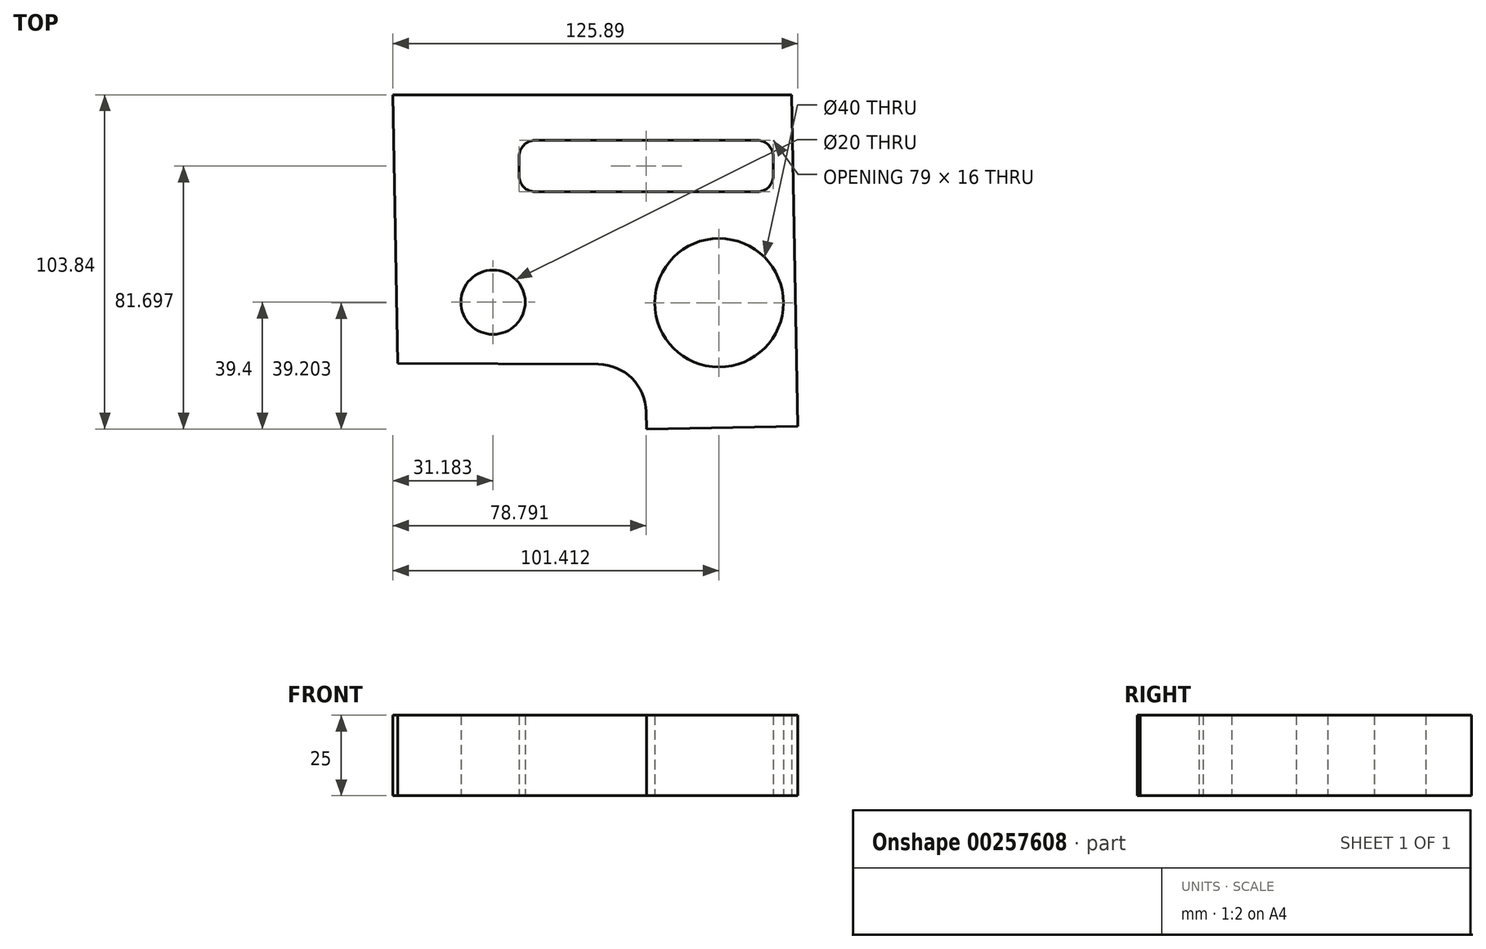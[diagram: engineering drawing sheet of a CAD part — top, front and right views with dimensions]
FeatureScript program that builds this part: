
annotation { "Feature Type Name" : "Feature", "Feature Type Description" : "" }
export const myFeature = defineFeature(function(context is Context, id is Id, definition is map)
    precondition{}
    {
        {
            var Q0;
            Q0=qCreatedBy(makeId("Top.planeOp"),FACE);
            var sketch = newSketch(context, id + "F0", { "sketchPlane" : qUnion([Q0])});
            skLineSegment(sketch, "E0", {"start": v(-101.89, 48.27) * mm, "end": v(22.11, 48.27) * mm});
            skLineSegment(sketch, "E1", {"start": v(22.11, 48.27) * mm, "end": v(24, -54.71) * mm});
            skPoint(sketch, "E2.visualSharp", {"position": v(-0.37, -35.15) * mm});
            skLineSegment(sketch, "E3", {"start": v(-101.89, 48.27) * mm, "end": v(-100.37, -35.15) * mm});
            skLineSegment(sketch, "E4", {"start": v(-101.89, 48.27) * mm, "end": v(-100.7, -16.72) * mm});
            skLineSegment(sketch, "E5", {"start": v(-100.7, -16.72) * mm, "end": v(-70.7, -16.17) * mm});
            skCircle(sketch, "E6", {"center": v(-70.7, -16.17) * mm, "radius": 10 * mm});
            skLineSegment(sketch, "E7", {"start": v(22.11, 48.27) * mm, "end": v(22.66, 18.28) * mm});
            skLineSegment(sketch, "E8", {"start": v(22.11, 48.27) * mm, "end": v(17.16, 48.27) * mm});
            skLineSegment(sketch, "E9", {"start": v(22.11, 48.27) * mm, "end": v(22.37, 34.27) * mm});
            skLineSegment(sketch, "E10", {"start": v(16.4, 29.13) * mm, "end": v(16.4, 23.13) * mm});
            skLineSegment(sketch, "E11", {"start": v(11.4, 18.13) * mm, "end": v(-57.6, 18.13) * mm});
            skLineSegment(sketch, "E12", {"start": v(11.4, 34.13) * mm, "end": v(-57.6, 34.13) * mm});
            skLineSegment(sketch, "E13", {"start": v(-62.6, 29.13) * mm, "end": v(-62.6, 23.13) * mm});
            skPoint(sketch, "E14.visualSharp", {"position": v(-62.6, 34.13) * mm});
            skArc(sketch, "E14.filletArc", {"start": v(-57.6, 34.13) * mm, "mid": v(-61.13, 32.66) * mm, "end": v(-62.6, 29.13) * mm});
            skPoint(sketch, "E15.visualSharp", {"position": v(-62.6, 18.13) * mm});
            skArc(sketch, "E15.filletArc", {"start": v(-62.6, 23.13) * mm, "mid": v(-61.13, 19.6) * mm, "end": v(-57.6, 18.13) * mm});
            skPoint(sketch, "E16.visualSharp", {"position": v(16.4, 34.13) * mm});
            skArc(sketch, "E16.filletArc", {"start": v(16.4, 29.13) * mm, "mid": v(14.94, 32.66) * mm, "end": v(11.4, 34.13) * mm});
            skPoint(sketch, "E17.visualSharp", {"position": v(16.4, 18.13) * mm});
            skArc(sketch, "E17.filletArc", {"start": v(11.4, 18.13) * mm, "mid": v(14.94, 19.6) * mm, "end": v(16.4, 23.13) * mm});
            skCircle(sketch, "E18", {"center": v(-0.48, -16.37) * mm, "radius": 20 * mm});
            skLineSegment(sketch, "E19", {"start": v(24, -54.71) * mm, "end": v(-23, -55.57) * mm});
            skLineSegment(sketch, "E20", {"start": v(-23, -55.57) * mm, "end": v(-23.1, -50.22) * mm});
            skLineSegment(sketch, "E21", {"start": v(-38, -35.5) * mm, "end": v(-100.37, -35.15) * mm});
            skPoint(sketch, "E22.visualSharp", {"position": v(-23.36, -35.57) * mm});
            skArc(sketch, "E22.filletArc", {"start": v(-23.1, -50.22) * mm, "mid": v(-27.55, -39.82) * mm, "end": v(-38, -35.5) * mm});
            skSolve(sketch);
        }
        {
            var Q0;
            Q0 = qSketchRegion(id + "F0", true);
            extrude(context, id + "F1", {"entities" : qUnion([Q0]), "depth" : 25 * mm});
        }
    });
